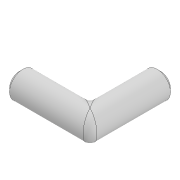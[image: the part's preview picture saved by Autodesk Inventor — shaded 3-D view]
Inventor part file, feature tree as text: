
AUTODESK INVENTOR PART (.ipt)
format: ipt  version: 2021 (Build 250183000, 183)  size: 152,064 bytes
history: native  units: mm
features: other x4, sketch x2, revolve x1, mirror x1, fillet x1
ambient origin geometry x8: Origin, YZ Plane, XZ Plane, XY Plane, X Axis, Y Axis, Z Axis, Center Point
bodies: Body1 (feature_tree)
feature tree (9):
  other  "Твердое тело1"
  revolve  "Вращение1"
  other  "РабПлоскость1"
  sketch  "Эскиз2"
  other  "РабПлоскость2"
  other  "Разделение1"
  mirror  "Зеркальное отражение1"
  fillet  "Сопряжение1"  [1 undecoded]
  sketch  "Эскиз1"
note: 1 required parameter value undecoded (feature->parameter linkage not recoverable at this tier; creation-order binding heuristic only, values carry confidence <= 0.55)
